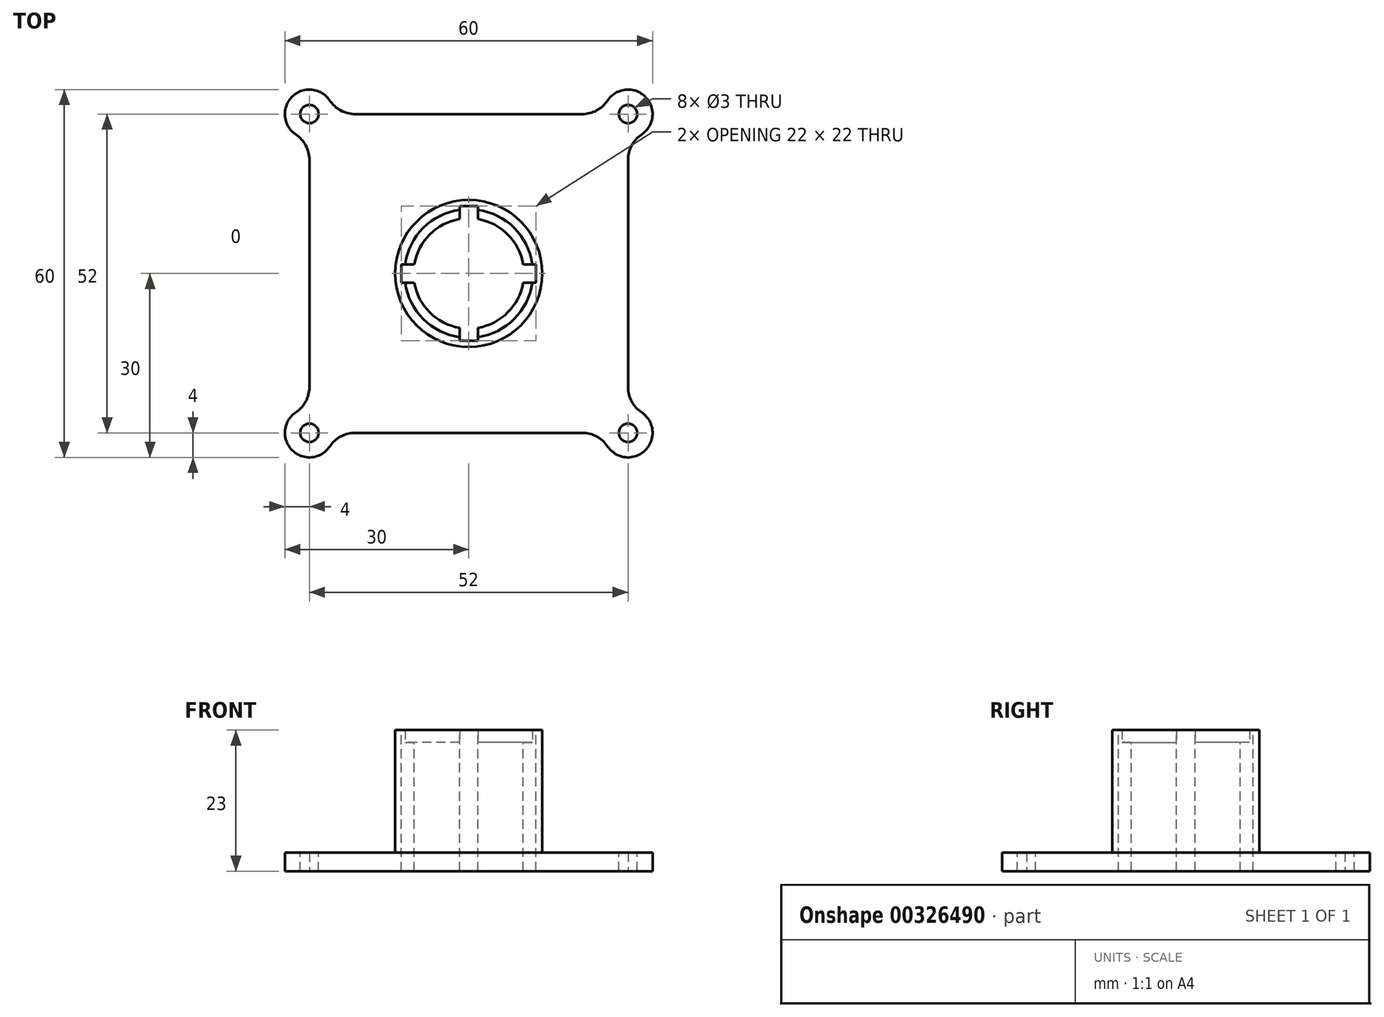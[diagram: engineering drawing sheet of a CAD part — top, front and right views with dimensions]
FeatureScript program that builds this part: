
annotation { "Feature Type Name" : "Feature", "Feature Type Description" : "" }
export const myFeature = defineFeature(function(context is Context, id is Id, definition is map)
    precondition{}
    {
        {
            var Q0;
            Q0=qCreatedBy(makeId("Top.planeOp"),FACE);
            var sketch = newSketch(context, id + "F0", { "sketchPlane" : qUnion([Q0])});
            skLineSegment(sketch, "E0", {"start": v(0, 0) * mm, "end": v(0, 30) * mm, "construction": true});
            skLineSegment(sketch, "E1", {"start": v(0, 0) * mm, "end": v(-30, 0) * mm, "construction": true});
            skLineSegment(sketch, "E2.0", {"start": v(-26, 18.52) * mm, "end": v(-26, -18.52) * mm});
            skLineSegment(sketch, "E2.1", {"start": v(-18.52, 26) * mm, "end": v(18.52, 26) * mm});
            skLineSegment(sketch, "E2.2", {"start": v(26, 18.52) * mm, "end": v(26, -18.52) * mm});
            skLineSegment(sketch, "E2.3", {"start": v(-18.52, -26) * mm, "end": v(18.52, -26) * mm});
            skArc(sketch, "E3", {"start": v(-22.67, 28.22) * mm, "mid": v(-28.83, 28.83) * mm, "end": v(-28.22, 22.67) * mm});
            skArc(sketch, "E4", {"start": v(28.22, 22.67) * mm, "mid": v(28.83, 28.83) * mm, "end": v(22.67, 28.22) * mm});
            skArc(sketch, "E5", {"start": v(22.67, -28.22) * mm, "mid": v(28.83, -28.83) * mm, "end": v(28.22, -22.67) * mm});
            skArc(sketch, "E6", {"start": v(-28.22, -22.67) * mm, "mid": v(-28.83, -28.83) * mm, "end": v(-22.67, -28.22) * mm});
            skPoint(sketch, "E7.visualSharp", {"position": v(-22, -26) * mm});
            skArc(sketch, "E7.filletArc", {"start": v(-18.52, -26) * mm, "mid": v(-20.87, -26.6) * mm, "end": v(-22.67, -28.22) * mm});
            skPoint(sketch, "E8.visualSharp", {"position": v(-26, -22) * mm});
            skArc(sketch, "E8.filletArc", {"start": v(-28.22, -22.67) * mm, "mid": v(-26.6, -20.87) * mm, "end": v(-26, -18.52) * mm});
            skPoint(sketch, "E9.visualSharp", {"position": v(-26, 22) * mm});
            skArc(sketch, "E9.filletArc", {"start": v(-26, 18.52) * mm, "mid": v(-26.6, 20.87) * mm, "end": v(-28.22, 22.67) * mm});
            skPoint(sketch, "E10.visualSharp", {"position": v(-22, 26) * mm});
            skArc(sketch, "E10.filletArc", {"start": v(-22.67, 28.22) * mm, "mid": v(-20.87, 26.6) * mm, "end": v(-18.52, 26) * mm});
            skPoint(sketch, "E11.visualSharp", {"position": v(22, 26) * mm});
            skArc(sketch, "E11.filletArc", {"start": v(18.52, 26) * mm, "mid": v(20.87, 26.6) * mm, "end": v(22.67, 28.22) * mm});
            skPoint(sketch, "E12.visualSharp", {"position": v(26, 22) * mm});
            skArc(sketch, "E12.filletArc", {"start": v(28.22, 22.67) * mm, "mid": v(26.6, 20.87) * mm, "end": v(26, 18.52) * mm});
            skPoint(sketch, "E13.visualSharp", {"position": v(26, -22) * mm});
            skArc(sketch, "E13.filletArc", {"start": v(26, -18.52) * mm, "mid": v(26.6, -20.87) * mm, "end": v(28.22, -22.67) * mm});
            skPoint(sketch, "E14.visualSharp", {"position": v(22, -26) * mm});
            skArc(sketch, "E14.filletArc", {"start": v(22.67, -28.22) * mm, "mid": v(20.87, -26.6) * mm, "end": v(18.52, -26) * mm});
            skSolve(sketch);
        }
        {
            var Q0;
            {var subQ9=sQuery(id+"F0.wireOp",EDGE,"E2.0");var subQ11=sQuery(id+"F0.wireOp",EDGE,"E3");var subQ15=makeQuery(id+"F0.imprint","INTERSECT",VERTEX,{"derivedFrom":[subQ9,subQ11]});Q0=makeQuery(id+"F0.imprint","IMPRINT",FACE,{"disambiguationData":[TD([[makeQuery(id+"F0.imprint","IMPRINT",EDGE,{"disambiguationData":[TD([[subQ15,-1.0]])],"derivedFrom":subQ9}),1.0]])]});}
            var Q1;
            {var subQ0=sQuery(id+"F0.wireOp",EDGE,"E2.1");var subQ1=sQuery(id+"F0.wireOp",EDGE,"E2.0");var subQ2=makeQuery(id+"F0.imprint","INTERSECT",VERTEX,{"derivedFrom":[subQ1,subQ0]});Q1=makeQuery(id+"F0.imprint","IMPRINT",FACE,{"disambiguationData":[TD([[makeQuery(id+"F0.imprint","IMPRINT",EDGE,{"disambiguationData":[TD([[subQ2,-1.0]])],"derivedFrom":subQ1}),-1.0]])]});}
            var Q2;
            {var subQ0=sQuery(id+"F0.wireOp",EDGE,"E2.3");var subQ1=sQuery(id+"F0.wireOp",EDGE,"E2.2");var subQ2=makeQuery(id+"F0.imprint","INTERSECT",VERTEX,{"derivedFrom":[subQ1,subQ0]});Q2=makeQuery(id+"F0.imprint","IMPRINT",FACE,{"disambiguationData":[TD([[makeQuery(id+"F0.imprint","IMPRINT",EDGE,{"disambiguationData":[TD([[subQ2,1.0]])],"derivedFrom":subQ1}),1.0]])]});}
            var Q3;
            {var subQ0=sQuery(id+"F0.wireOp",EDGE,"E2.3");var subQ1=sQuery(id+"F0.wireOp",EDGE,"E2.0");var subQ2=makeQuery(id+"F0.imprint","INTERSECT",VERTEX,{"derivedFrom":[subQ1,subQ0]});Q3=makeQuery(id+"F0.imprint","IMPRINT",FACE,{"disambiguationData":[TD([[makeQuery(id+"F0.imprint","IMPRINT",EDGE,{"disambiguationData":[TD([[subQ2,1.0]])],"derivedFrom":subQ1}),-1.0]])]});}
            var Q4;
            {var subQ0=sQuery(id+"F0.wireOp",EDGE,"E2.3");var subQ1=sQuery(id+"F0.wireOp",EDGE,"E2.0");var subQ2=makeQuery(id+"F0.imprint","INTERSECT",VERTEX,{"derivedFrom":[subQ1,subQ0]});Q4=makeQuery(id+"F0.imprint","IMPRINT",FACE,{"disambiguationData":[TD([[makeQuery(id+"F0.imprint","IMPRINT",EDGE,{"disambiguationData":[TD([[subQ2,1.0]])],"derivedFrom":subQ1}),1.0]])]});}
            var Q5;
            {var subQ0=sQuery(id+"F0.wireOp",EDGE,"E2.1");var subQ1=sQuery(id+"F0.wireOp",EDGE,"E2.0");var subQ2=makeQuery(id+"F0.imprint","INTERSECT",VERTEX,{"derivedFrom":[subQ1,subQ0]});Q5=makeQuery(id+"F0.imprint","IMPRINT",FACE,{"disambiguationData":[TD([[makeQuery(id+"F0.imprint","IMPRINT",EDGE,{"disambiguationData":[TD([[subQ2,-1.0]])],"derivedFrom":subQ1}),1.0]])]});}
            var Q6;
            {var subQ0=sQuery(id+"F0.wireOp",EDGE,"E2.3");var subQ1=sQuery(id+"F0.wireOp",EDGE,"E2.2");var subQ2=makeQuery(id+"F0.imprint","INTERSECT",VERTEX,{"derivedFrom":[subQ1,subQ0]});Q6=makeQuery(id+"F0.imprint","IMPRINT",FACE,{"disambiguationData":[TD([[makeQuery(id+"F0.imprint","IMPRINT",EDGE,{"disambiguationData":[TD([[subQ2,1.0]])],"derivedFrom":subQ1}),-1.0]])]});}
            var Q7;
            {var subQ0=sQuery(id+"F0.wireOp",EDGE,"E2.2");var subQ1=sQuery(id+"F0.wireOp",EDGE,"E2.1");var subQ2=makeQuery(id+"F0.imprint","INTERSECT",VERTEX,{"derivedFrom":[subQ1,subQ0]});Q7=makeQuery(id+"F0.imprint","IMPRINT",FACE,{"disambiguationData":[TD([[makeQuery(id+"F0.imprint","IMPRINT",EDGE,{"disambiguationData":[TD([[subQ2,1.0]])],"derivedFrom":subQ1}),-1.0]])]});}
            var Q8;
            {var subQ0=sQuery(id+"F0.wireOp",EDGE,"E2.2");var subQ1=sQuery(id+"F0.wireOp",EDGE,"E2.1");var subQ2=makeQuery(id+"F0.imprint","INTERSECT",VERTEX,{"derivedFrom":[subQ1,subQ0]});Q8=makeQuery(id+"F0.imprint","IMPRINT",FACE,{"disambiguationData":[TD([[makeQuery(id+"F0.imprint","IMPRINT",EDGE,{"disambiguationData":[TD([[subQ2,1.0]])],"derivedFrom":subQ1}),1.0]])]});}
            extrude(context, id + "F1", {"entities" : qUnion([Q0, Q1, Q2, Q3, Q4, Q5, Q6, Q7, Q8]), "depth" : 3 * mm});
        }
        {
            var Q0;
            Q0=makeQuery(id+"F1.opExtrude","CAP_FACE",FACE,{"disambiguationData":[OSD([sQuery(id+"F0.wireOp",EDGE,"E2.0"),sQuery(id+"F0.wireOp",EDGE,"E2.1"),sQuery(id+"F0.wireOp",EDGE,"E2.2"),sQuery(id+"F0.wireOp",EDGE,"E2.3"),sQuery(id+"F0.wireOp",EDGE,"E3"),sQuery(id+"F0.wireOp",EDGE,"E4"),sQuery(id+"F0.wireOp",EDGE,"E5"),sQuery(id+"F0.wireOp",EDGE,"E6"),sQuery(id+"F0.wireOp",EDGE,"E7.filletArc"),sQuery(id+"F0.wireOp",EDGE,"E8.filletArc"),sQuery(id+"F0.wireOp",EDGE,"E9.filletArc"),sQuery(id+"F0.wireOp",EDGE,"E10.filletArc"),sQuery(id+"F0.wireOp",EDGE,"E11.filletArc"),sQuery(id+"F0.wireOp",EDGE,"E12.filletArc"),sQuery(id+"F0.wireOp",EDGE,"E13.filletArc"),sQuery(id+"F0.wireOp",EDGE,"E14.filletArc")])],"isStart":false});
            var sketch = newSketch(context, id + "F2", { "sketchPlane" : qUnion([Q0])});
            skPoint(sketch, "E15", {"position": v(26, 26) * mm});
            skPoint(sketch, "E16", {"position": v(-26, 26) * mm});
            skPoint(sketch, "E17", {"position": v(-26, -26) * mm});
            skPoint(sketch, "E18", {"position": v(26, -26) * mm});
            skCircle(sketch, "E19", {"center": v(0, 0) * mm, "radius": 9 * mm});
            skCircle(sketch, "E20", {"center": v(0, 0) * mm, "radius": 10.5 * mm});
            skCircle(sketch, "E21", {"center": v(0, 0) * mm, "radius": 12 * mm});
            skSolve(sketch);
        }
        {
            var Q0;
            Q0=sQuery(id+"F2.wireOp",VERTEX,"E15");
            var Q1;
            Q1=sQuery(id+"F2.wireOp",VERTEX,"E16");
            var Q2;
            Q2=sQuery(id+"F2.wireOp",VERTEX,"E17");
            var Q3;
            Q3=sQuery(id+"F2.wireOp",VERTEX,"E18");
            var Q4;
            Q4=makeQuery(id+"F1.opExtrude","SWEPT_BODY",BODY,{"disambiguationData":[OSD([sQuery(id+"F0.wireOp",EDGE,"E2.0"),sQuery(id+"F0.wireOp",EDGE,"E2.1"),sQuery(id+"F0.wireOp",EDGE,"E2.2"),sQuery(id+"F0.wireOp",EDGE,"E2.3"),sQuery(id+"F0.wireOp",EDGE,"E3"),sQuery(id+"F0.wireOp",EDGE,"E4"),sQuery(id+"F0.wireOp",EDGE,"E5"),sQuery(id+"F0.wireOp",EDGE,"E6"),sQuery(id+"F0.wireOp",EDGE,"E7.filletArc"),sQuery(id+"F0.wireOp",EDGE,"E8.filletArc"),sQuery(id+"F0.wireOp",EDGE,"E9.filletArc"),sQuery(id+"F0.wireOp",EDGE,"E10.filletArc"),sQuery(id+"F0.wireOp",EDGE,"E11.filletArc"),sQuery(id+"F0.wireOp",EDGE,"E12.filletArc"),sQuery(id+"F0.wireOp",EDGE,"E13.filletArc"),sQuery(id+"F0.wireOp",EDGE,"E14.filletArc")])]});
            hole(context, id + "F3", {"style" : HoleStyle.SIMPLE, "endStyle" : HoleEndStyle.THROUGH, "holeDiameter" : 3 * mm, "tappedDepth" : 12 * mm, "tapClearance" : 3, "locations" : qUnion([Q0, Q1, Q2, Q3]), "scope" : qUnion([Q4])});
        }
        {
            var Q0;
            Q0=sQuery(id+"F2.wireOp",VERTEX,"E19.center");
            var Q1;
            Q1=makeQuery(id+"F1.opExtrude","SWEPT_BODY",BODY,{"disambiguationData":[OSD([sQuery(id+"F0.wireOp",EDGE,"E2.0"),sQuery(id+"F0.wireOp",EDGE,"E2.1"),sQuery(id+"F0.wireOp",EDGE,"E2.2"),sQuery(id+"F0.wireOp",EDGE,"E2.3"),sQuery(id+"F0.wireOp",EDGE,"E3"),sQuery(id+"F0.wireOp",EDGE,"E4"),sQuery(id+"F0.wireOp",EDGE,"E5"),sQuery(id+"F0.wireOp",EDGE,"E6"),sQuery(id+"F0.wireOp",EDGE,"E7.filletArc"),sQuery(id+"F0.wireOp",EDGE,"E8.filletArc"),sQuery(id+"F0.wireOp",EDGE,"E9.filletArc"),sQuery(id+"F0.wireOp",EDGE,"E10.filletArc"),sQuery(id+"F0.wireOp",EDGE,"E11.filletArc"),sQuery(id+"F0.wireOp",EDGE,"E12.filletArc"),sQuery(id+"F0.wireOp",EDGE,"E13.filletArc"),sQuery(id+"F0.wireOp",EDGE,"E14.filletArc")])]});
            hole(context, id + "F4", {"style" : HoleStyle.SIMPLE, "endStyle" : HoleEndStyle.THROUGH, "holeDiameter" : 18 * mm, "tappedDepth" : 12 * mm, "tapClearance" : 3, "locations" : qUnion([Q0]), "scope" : qUnion([Q1])});
        }
        {
            var Q0;
            Q0=makeQuery(id+"F2.imprint","IMPRINT",FACE,{"disambiguationData":[TD([[makeQuery(id+"F2.imprint","IMPRINT",EDGE,{"derivedFrom":sQuery(id+"F2.wireOp",EDGE,"E19")}),-1.0]])]});
            extrude(context, id + "F5", {"entities" : qUnion([Q0]), "operationType" : NewBodyOperationType.ADD, "depth" : 18 * mm});
        }
        {
            var Q0;
            Q0=makeQuery(id+"F2.imprint","IMPRINT",FACE,{"disambiguationData":[TD([[makeQuery(id+"F2.imprint","IMPRINT",EDGE,{"derivedFrom":sQuery(id+"F2.wireOp",EDGE,"E20")}),-1.0]])]});
            extrude(context, id + "F6", {"entities" : qUnion([Q0]), "operationType" : NewBodyOperationType.ADD, "depth" : 20 * mm});
        }
        {
            var Q0;
            Q0=makeQuery(id+"F6.opExtrude","CAP_FACE",FACE,{"disambiguationData":[OSD([sQuery(id+"F2.wireOp",EDGE,"E20"),sQuery(id+"F2.wireOp",EDGE,"E21")])],"isStart":false});
            var sketch = newSketch(context, id + "F7", { "sketchPlane" : qUnion([Q0])});
            skLineSegment(sketch, "E22.bottom", {"start": v(-11, 1.5) * mm, "end": v(11, 1.5) * mm});
            skLineSegment(sketch, "E22.top", {"start": v(-11, -1.5) * mm, "end": v(11, -1.5) * mm});
            skLineSegment(sketch, "E22.left", {"start": v(-11, 1.5) * mm, "end": v(-11, -1.5) * mm});
            skLineSegment(sketch, "E22.right", {"start": v(11, 1.5) * mm, "end": v(11, -1.5) * mm});
            skLineSegment(sketch, "E23", {"start": v(0, 0) * mm, "end": v(0, 1.5) * mm, "construction": true});
            skLineSegment(sketch, "E24", {"start": v(0, 0) * mm, "end": v(11, 0) * mm, "construction": true});
            skLineSegment(sketch, "E25.1.0", {"start": v(-1.5, 11) * mm, "end": v(-1.5, -11) * mm});
            skLineSegment(sketch, "E25.1.1", {"start": v(1.5, 11) * mm, "end": v(-1.5, 11) * mm});
            skLineSegment(sketch, "E25.1.2", {"start": v(1.5, 11) * mm, "end": v(1.5, -11) * mm});
            skLineSegment(sketch, "E25.1.3", {"start": v(1.5, -11) * mm, "end": v(-1.5, -11) * mm});
            skPoint(sketch, "E25.center", {"position": v(0, 0) * mm});
            skLineSegment(sketch, "E25.anchor1", {"start": v(0, 0) * mm, "end": v(-11, -1.5) * mm, "construction": true});
            skLineSegment(sketch, "E25.anchor2", {"start": v(0, 0) * mm, "end": v(-1.5, 11) * mm, "construction": true});
            skSolve(sketch);
        }
        {
            var Q0;
            {var subQ0=sQuery(id+"F7.wireOp",EDGE,"E22.left");Q0=makeQuery(id+"F7.imprint","IMPRINT",FACE,{"disambiguationData":[TD([[makeQuery(id+"F7.imprint","IMPRINT",EDGE,{"derivedFrom":subQ0}),1.0]])]});}
            var Q1;
            {var subQ0=sQuery(id+"F7.wireOp",EDGE,"E25.1.0");var subQ1=sQuery(id+"F7.wireOp",EDGE,"E22.bottom");var subQ2=makeQuery(id+"F7.imprint","INTERSECT",VERTEX,{"derivedFrom":[subQ1,subQ0]});Q1=makeQuery(id+"F7.imprint","IMPRINT",FACE,{"disambiguationData":[TD([[makeQuery(id+"F7.imprint","IMPRINT",EDGE,{"disambiguationData":[TD([[subQ2,1.0]])],"derivedFrom":subQ1}),-1.0]])]});}
            var Q2;
            {var subQ0=sQuery(id+"F7.wireOp",EDGE,"E25.1.0");var subQ1=sQuery(id+"F7.wireOp",EDGE,"E22.top");var subQ2=makeQuery(id+"F7.imprint","INTERSECT",VERTEX,{"derivedFrom":[subQ1,subQ0]});Q2=makeQuery(id+"F7.imprint","IMPRINT",FACE,{"disambiguationData":[TD([[makeQuery(id+"F7.imprint","IMPRINT",EDGE,{"disambiguationData":[TD([[subQ2,-1.0]])],"derivedFrom":subQ1}),-1.0]])]});}
            var Q3;
            {var subQ0=sQuery(id+"F7.wireOp",EDGE,"E25.1.3");Q3=makeQuery(id+"F7.imprint","IMPRINT",FACE,{"disambiguationData":[TD([[makeQuery(id+"F7.imprint","IMPRINT",EDGE,{"derivedFrom":subQ0}),-1.0]])]});}
            var Q4;
            {var subQ0=sQuery(id+"F7.wireOp",EDGE,"E25.1.2");var subQ1=sQuery(id+"F7.wireOp",EDGE,"E22.bottom");var subQ2=makeQuery(id+"F7.imprint","INTERSECT",VERTEX,{"derivedFrom":[subQ1,subQ0]});Q4=makeQuery(id+"F7.imprint","IMPRINT",FACE,{"disambiguationData":[TD([[makeQuery(id+"F7.imprint","IMPRINT",EDGE,{"disambiguationData":[TD([[subQ2,-1.0]])],"derivedFrom":subQ1}),-1.0]])]});}
            var Q5;
            {var subQ0=sQuery(id+"F7.wireOp",EDGE,"E22.right");Q5=makeQuery(id+"F7.imprint","IMPRINT",FACE,{"disambiguationData":[TD([[makeQuery(id+"F7.imprint","IMPRINT",EDGE,{"derivedFrom":subQ0}),-1.0]])]});}
            var Q6;
            {var subQ0=sQuery(id+"F7.wireOp",EDGE,"E25.1.0");var subQ1=sQuery(id+"F7.wireOp",EDGE,"E22.bottom");var subQ2=makeQuery(id+"F7.imprint","INTERSECT",VERTEX,{"derivedFrom":[subQ1,subQ0]});Q6=makeQuery(id+"F7.imprint","IMPRINT",FACE,{"disambiguationData":[TD([[makeQuery(id+"F7.imprint","IMPRINT",EDGE,{"disambiguationData":[TD([[subQ2,-1.0]])],"derivedFrom":subQ1}),1.0]])]});}
            var Q7;
            {var subQ0=sQuery(id+"F7.wireOp",EDGE,"E25.1.1");Q7=makeQuery(id+"F7.imprint","IMPRINT",FACE,{"disambiguationData":[TD([[makeQuery(id+"F7.imprint","IMPRINT",EDGE,{"derivedFrom":subQ0}),1.0]])]});}
            extrude(context, id + "F8", {"entities" : qUnion([Q0, Q1, Q2, Q3, Q4, Q5, Q6, Q7]), "operationType" : NewBodyOperationType.REMOVE, "endBound" : BoundingType.THROUGH_ALL, "oppositeDirection" : true, "depth" : 25 * mm});
        }
        {
            var Q0;
            Q0=makeQuery(id+"F1.opExtrude","SWEPT_BODY",BODY,{"disambiguationData":[OSD([sQuery(id+"F0.wireOp",EDGE,"E2.0"),sQuery(id+"F0.wireOp",EDGE,"E2.1"),sQuery(id+"F0.wireOp",EDGE,"E2.2"),sQuery(id+"F0.wireOp",EDGE,"E2.3"),sQuery(id+"F0.wireOp",EDGE,"E3"),sQuery(id+"F0.wireOp",EDGE,"E4"),sQuery(id+"F0.wireOp",EDGE,"E5"),sQuery(id+"F0.wireOp",EDGE,"E6"),sQuery(id+"F0.wireOp",EDGE,"E7.filletArc"),sQuery(id+"F0.wireOp",EDGE,"E8.filletArc"),sQuery(id+"F0.wireOp",EDGE,"E9.filletArc"),sQuery(id+"F0.wireOp",EDGE,"E10.filletArc"),sQuery(id+"F0.wireOp",EDGE,"E11.filletArc"),sQuery(id+"F0.wireOp",EDGE,"E12.filletArc"),sQuery(id+"F0.wireOp",EDGE,"E13.filletArc"),sQuery(id+"F0.wireOp",EDGE,"E14.filletArc")])]});
            transform(context, id + "F9", {"entities" : qUnion([Q0]), "transformType" : TransformType.TRANSLATION_3D, "dx" : 0 * mm, "dy" : 0 * mm, "dz" : 0 * mm, "makeCopy" : true});
        }
    });
